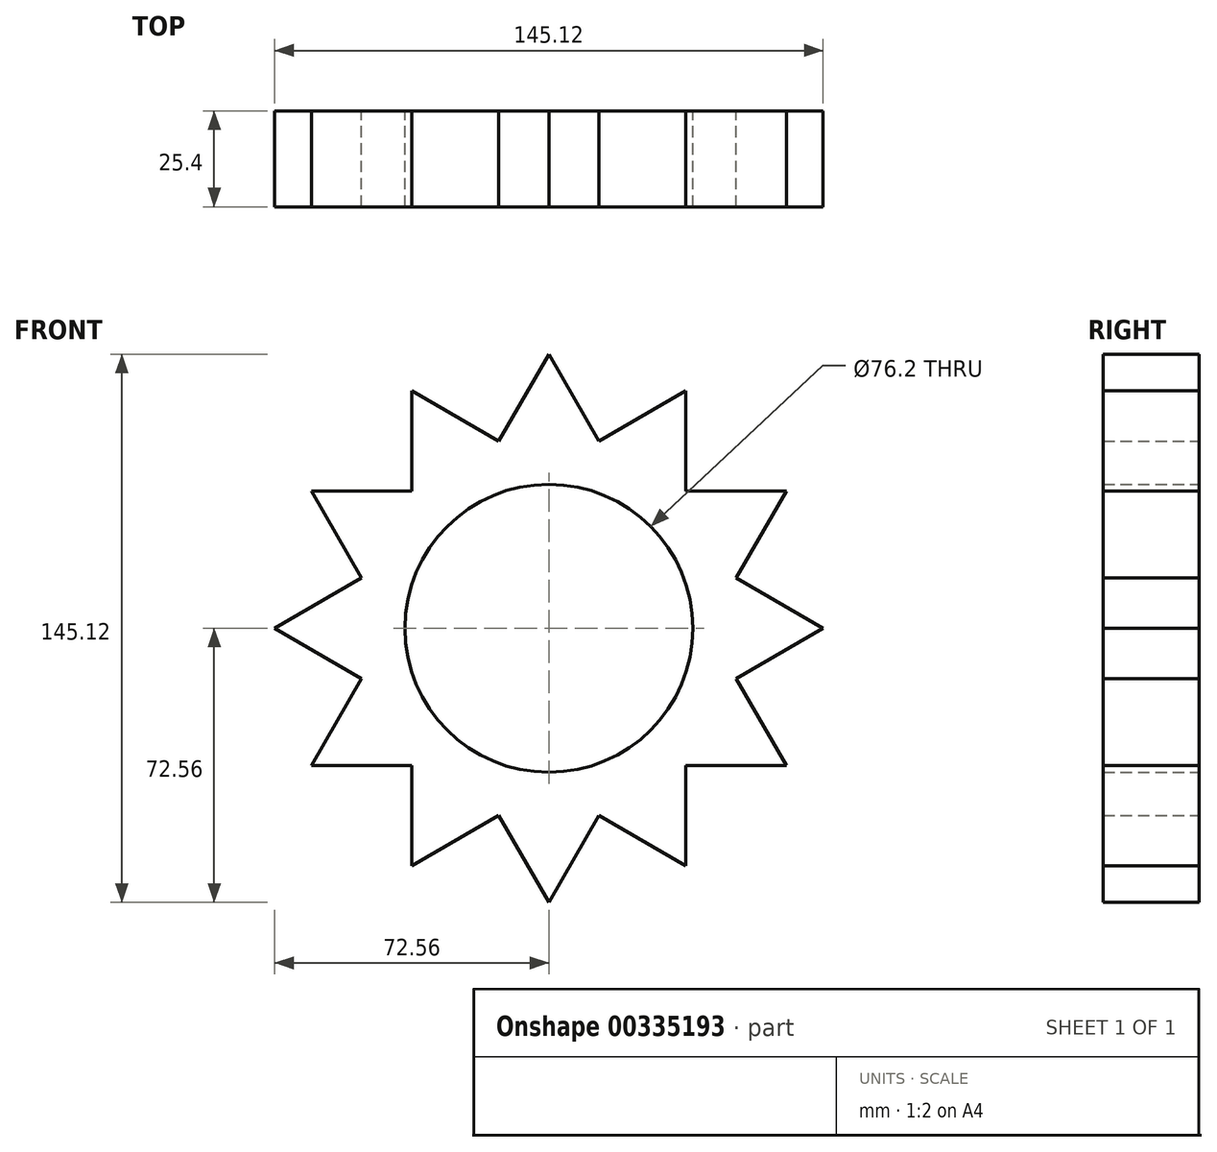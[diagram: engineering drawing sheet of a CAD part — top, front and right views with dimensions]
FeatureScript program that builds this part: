
annotation { "Feature Type Name" : "Feature", "Feature Type Description" : "" }
export const myFeature = defineFeature(function(context is Context, id is Id, definition is map)
    precondition{}
    {
        {
            var Q0;
            Q0=qCreatedBy(makeId("Front.planeOp"),FACE);
            var sketch = newSketch(context, id + "F0", { "sketchPlane" : qUnion([Q0])});
            skCircle(sketch, "E0", {"center": v(0, 0) * mm, "radius": 50.8 * mm});
            skCircle(sketch, "E1", {"center": v(0, 0) * mm, "radius": 38.1 * mm});
            skLineSegment(sketch, "E2", {"start": v(0, 72.56) * mm, "end": v(0, -70.78) * mm, "construction": true});
            skLineSegment(sketch, "E3", {"start": v(-65.47, 0) * mm, "end": v(65.57, 0) * mm, "construction": true});
            skLineSegment(sketch, "E4", {"start": v(0, 72.56) * mm, "end": v(-13.64, 48.93) * mm});
            skLineSegment(sketch, "E5.MirrorCS", {"start": v(0, 72.56) * mm, "end": v(13.64, 48.93) * mm});
            skLineSegment(sketch, "E6.anchor1", {"start": v(0, 0) * mm, "end": v(13.64, 48.93) * mm, "construction": true});
            skLineSegment(sketch, "E6.anchor2", {"start": v(0, 0) * mm, "end": v(13.64, 48.93) * mm, "construction": true});
            skLineSegment(sketch, "E7.1.0", {"start": v(-36.28, 62.84) * mm, "end": v(-12.65, 49.2) * mm});
            skLineSegment(sketch, "E7.1.1", {"start": v(-36.28, 62.84) * mm, "end": v(-36.28, 35.56) * mm});
            skLineSegment(sketch, "E7.2.0", {"start": v(-62.84, 36.28) * mm, "end": v(-35.56, 36.28) * mm});
            skLineSegment(sketch, "E7.2.1", {"start": v(-62.84, 36.28) * mm, "end": v(-49.2, 12.65) * mm});
            skLineSegment(sketch, "E7.3.0", {"start": v(-72.56, 0) * mm, "end": v(-48.93, 13.64) * mm});
            skLineSegment(sketch, "E7.3.1", {"start": v(-72.56, 0) * mm, "end": v(-48.93, -13.64) * mm});
            skLineSegment(sketch, "E7.4.0", {"start": v(-62.84, -36.28) * mm, "end": v(-49.2, -12.65) * mm});
            skLineSegment(sketch, "E7.4.1", {"start": v(-62.84, -36.28) * mm, "end": v(-35.56, -36.28) * mm});
            skLineSegment(sketch, "E7.5.0", {"start": v(-36.28, -62.84) * mm, "end": v(-36.28, -35.56) * mm});
            skLineSegment(sketch, "E7.5.1", {"start": v(-36.28, -62.84) * mm, "end": v(-12.65, -49.2) * mm});
            skLineSegment(sketch, "E7.6.0", {"start": v(0, -72.56) * mm, "end": v(-13.64, -48.93) * mm});
            skLineSegment(sketch, "E7.6.1", {"start": v(0, -72.56) * mm, "end": v(13.64, -48.93) * mm});
            skLineSegment(sketch, "E7.7.0", {"start": v(36.28, -62.84) * mm, "end": v(12.65, -49.2) * mm});
            skLineSegment(sketch, "E7.7.1", {"start": v(36.28, -62.84) * mm, "end": v(36.28, -35.56) * mm});
            skLineSegment(sketch, "E7.8.0", {"start": v(62.84, -36.28) * mm, "end": v(35.56, -36.28) * mm});
            skLineSegment(sketch, "E7.8.1", {"start": v(62.84, -36.28) * mm, "end": v(49.2, -12.65) * mm});
            skLineSegment(sketch, "E7.9.0", {"start": v(72.56, 0) * mm, "end": v(48.93, -13.64) * mm});
            skLineSegment(sketch, "E7.9.1", {"start": v(72.56, 0) * mm, "end": v(48.93, 13.64) * mm});
            skLineSegment(sketch, "E7.10.0", {"start": v(62.84, 36.28) * mm, "end": v(49.2, 12.65) * mm});
            skLineSegment(sketch, "E7.10.1", {"start": v(62.84, 36.28) * mm, "end": v(35.56, 36.28) * mm});
            skLineSegment(sketch, "E8.2.11.0", {"start": v(36.28, 62.84) * mm, "end": v(36.28, 35.56) * mm});
            skLineSegment(sketch, "E8.3.11.0", {"start": v(36.28, 62.84) * mm, "end": v(12.65, 49.2) * mm});
            skSolve(sketch);
        }
        {
            var Q0;
            Q0 = qSketchRegion(id + "F0", true);
            var Q1;
            Q1=makeQuery(id+"F0.imprint","IMPRINT",FACE,{"disambiguationData":[TD([[makeQuery(id+"F0.imprint","IMPRINT",EDGE,{"derivedFrom":sQuery(id+"F0.wireOp",EDGE,"E1")}),-1.0]])]});
            extrude(context, id + "F1", {"entities" : qUnion([Q0, Q1]), "depth" : 25.4 * mm});
        }
    });
